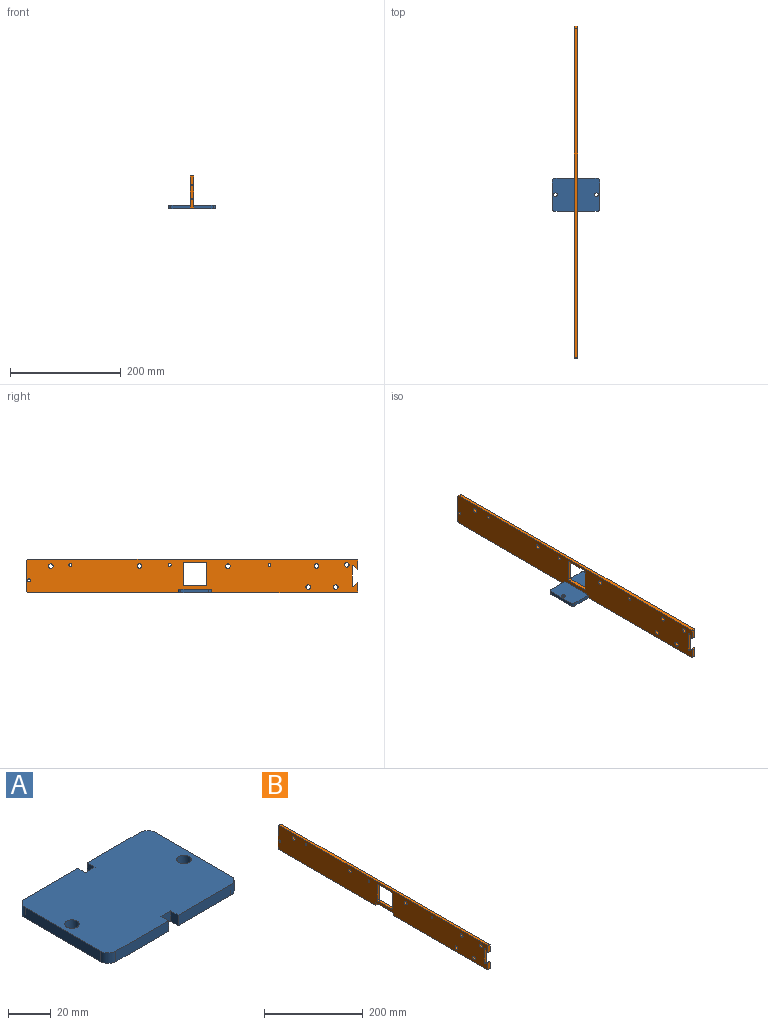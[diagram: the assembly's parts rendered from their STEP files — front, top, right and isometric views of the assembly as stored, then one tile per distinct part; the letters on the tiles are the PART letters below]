
ASSEMBLY  parts=2 mates=1
PART A: 20 faces, bbox 86x60x6 mm
  f0: plane 6x5mm, normal (-1,0,0), area 30mm2, adj f1,f13,f14,f15
  f1: plane 6.4x6mm, normal (0,-1,0), area 38.4mm2, adj f0,f2,f14,f15
  f2: plane 6x5mm, normal (1,0,0), area 30mm2, adj f1,f3,f14,f15
  f3: plane 34.8x6mm, normal (0,-1,0), area 208.8mm2, adj f2,f14,f15,f17
  f4: plane 50x6mm, normal (-1,0,0), area 300mm2, adj f14,f15,f16,f17
  f5: plane 34.8x6mm, normal (0,1,0), area 208.8mm2, adj f6,f14,f15,f16
  f6: plane 6x5mm, normal (1,0,0), area 30mm2, adj f5,f7,f14,f15
  f7: plane 6.4x6mm, normal (0,1,0), area 38.4mm2, adj f6,f8,f14,f15
  f8: plane 6x5mm, normal (-1,0,0), area 30mm2, adj f7,f9,f14,f15
  f9: plane 34.8x6mm, normal (0,1,0), area 208.8mm2, adj f8,f14,f15,f18
  f10: plane 50x6mm, normal (1,0,0), area 300mm2, adj f14,f15,f18,f19
  f11: cylinder r=3.4mm len=6.8mm, axis (0,0,-1), area 128.2mm2, adj f14,f15
  f12: cylinder r=3.4mm len=6.8mm, axis (0,0,-1), area 128.2mm2, adj f14,f15
  f13: plane 34.8x6mm, normal (0,-1,0), area 208.8mm2, adj f0,f14,f15,f19
  f14: plane 86x60mm, normal (0,0,-1), area 5001.9mm2, adj f0,f1,f2,f3,f4,f5,f6,f7
  f15: plane 86x60mm, normal (0,0,1), area 5001.9mm2, adj f0,f1,f2,f3,f4,f5,f6,f7
  f16: cylinder r=5mm len=6mm, axis (0,0,1), area 47.1mm2, adj f4,f5,f14,f15
  f17: cylinder r=5mm len=6mm, axis (0,0,-1), area 47.1mm2, adj f3,f4,f14,f15
  f18: cylinder r=5mm len=6mm, axis (0,0,-1), area 47.1mm2, adj f9,f10,f14,f15
  f19: cylinder r=5mm len=6mm, axis (0,0,1), area 47.1mm2, adj f10,f13,f14,f15
PART B: 41 faces, bbox 6x600x60 mm
  f0: plane 50x6mm, normal (0,0,-1), area 300mm2, adj f1,f26,f27,f28
  f1: plane 6x6mm, normal (0,1,0), area 36mm2, adj f0,f2,f27,f28
  f2: plane 268.95x6mm, normal (0,0,-1), area 1613.7mm2, adj f1,f27,f28,f31
  f3: plane 15.79x6mm, normal (0,-1,0), area 94.7mm2, adj f27,f28,f31,f40
  f4: plane 6.42x6.42mm, normal (0,0.71,0.71), area 54.4mm2, adj f27,f28,f38,f40
  f5: plane 36.29x6mm, normal (0,-1,0), area 217.7mm2, adj f27,f28,f38,f39
  f6: plane 6.42x6.42mm, normal (0,0.71,-0.71), area 54.4mm2, adj f27,f28,f33,f39
  f7: plane 15.79x6mm, normal (0,-1,0), area 94.7mm2, adj f27,f28,f32,f33
  f8: plane 593.95x6mm, normal (0,0,1), area 3563.7mm2, adj f27,f28,f30,f32
  f9: plane 50x6mm, normal (0,1,0), area 300mm2, adj f27,f28,f29,f30
  f10: plane 275x6mm, normal (0,0,-1), area 1650mm2, adj f26,f27,f28,f29
  f11: plane 38x6mm, normal (0,-1,0), area 228mm2, adj f27,f28,f35,f37
  f12: plane 38x6mm, normal (0,0,-1), area 228mm2, adj f27,f28,f34,f35
  f13: plane 38x6mm, normal (0,1,0), area 228mm2, adj f27,f28,f34,f36
  f14: cylinder r=2.65mm len=6mm, axis (1,0,0), area 99.9mm2, adj f27,f28
  f15: cylinder r=2.65mm len=6mm, axis (1,0,0), area 99.9mm2, adj f27,f28
  f16: cylinder r=2.65mm len=6mm, axis (1,0,0), area 99.9mm2, adj f27,f28
  f17: cylinder r=2.65mm len=6mm, axis (1,0,0), area 99.9mm2, adj f27,f28
  f18: cylinder r=4.05mm len=8.1mm, axis (1,0,0), area 152.7mm2, adj f27,f28
  f19: cylinder r=4.05mm len=8.1mm, axis (1,0,0), area 152.7mm2, adj f27,f28
  f20: cylinder r=4.05mm len=8.1mm, axis (1,0,0), area 152.7mm2, adj f27,f28
  f21: cylinder r=4.05mm len=8.1mm, axis (1,0,0), area 152.7mm2, adj f27,f28
  f22: cylinder r=4.05mm len=8.1mm, axis (1,0,0), area 152.7mm2, adj f27,f28
  f23: cylinder r=4.05mm len=8.1mm, axis (1,0,0), area 152.7mm2, adj f27,f28
  f24: cylinder r=4.05mm len=8.1mm, axis (1,0,0), area 152.7mm2, adj f27,f28
  f25: plane 38x6mm, normal (0,0,1), area 228mm2, adj f27,f28,f36,f37
  f26: plane 6x6mm, normal (0,-1,0), area 36mm2, adj f0,f10,f27,f28
  f27: plane 599.95x60mm, normal (-1,0,0), area 33160.9mm2, adj f0,f1,f2,f3,f4,f5,f6,f7
  f28: plane 599.95x60mm, normal (1,0,0), area 33160.9mm2, adj f0,f1,f2,f3,f4,f5,f6,f7
  f29: cylinder r=5mm len=6mm, axis (1,0,0), area 47.1mm2, adj f9,f10,f27,f28
  f30: cylinder r=5mm len=6mm, axis (-1,0,0), area 47.1mm2, adj f8,f9,f27,f28
  f31: cylinder r=1mm len=6mm, axis (1,0,0), area 9.4mm2, adj f2,f3,f27,f28
  f32: cylinder r=1mm len=6mm, axis (-1,0,0), area 9.4mm2, adj f7,f8,f27,f28
  f33: cylinder r=1mm len=6mm, axis (-1,0,0), area 14.1mm2, adj f6,f7,f27,f28
  f34: cylinder r=2mm len=6mm, axis (-1,0,0), area 18.8mm2, adj f12,f13,f27,f28
  f35: cylinder r=2mm len=6mm, axis (1,0,0), area 18.8mm2, adj f11,f12,f27,f28
  f36: cylinder r=2mm len=6mm, axis (1,0,0), area 18.8mm2, adj f13,f25,f27,f28
  f37: cylinder r=2mm len=6mm, axis (-1,0,0), area 18.8mm2, adj f11,f25,f27,f28
  f38: cylinder r=1.1mm len=6mm, axis (-1,0,0), area 15.6mm2, adj f4,f5,f27,f28
  f39: cylinder r=1.1mm len=6mm, axis (1,0,0), area 15.6mm2, adj f5,f6,f27,f28
  f40: cylinder r=1mm len=6mm, axis (1,0,0), area 14.1mm2, adj f3,f4,f27,f28
PLACE A at identity
PLACE B at identity fixed
MATE fastened A.f15 <-> B.f0  axis (0,0,1) through (3,300,-29)mm
